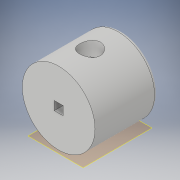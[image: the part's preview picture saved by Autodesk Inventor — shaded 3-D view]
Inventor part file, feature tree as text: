
AUTODESK INVENTOR PART (.ipt)
format: ipt  version: 2017 (Build 210142000, 142)  size: 147,456 bytes
history: native  units: in
note: dims shown in document units (in); Inventor stores cm internally (conversion verified against a paired STEP export)
features: sketch x4, extrude x2, plane x2, hole x2, chamfer x1, fillet x1
ambient origin geometry x8: Origin, YZ Plane, XZ Plane, XY Plane, X Axis, Y Axis, Z Axis, Center Point
bodies: Solid1 (feature_tree)
feature tree (12):
  extrude  "Extrusion1"  Depth=1.0in TaperAngle=0.0deg
  plane  "Work Plane2"
  sketch  "Sketch2"  dims[d3=0.5in d4=0.0in]
  sketch  "Sketch3"  dims[d5=0.5in d6=0.0in]
  hole  "Hole1"  [1 undecoded]
  hole  "Hole2"  [1 undecoded]
  extrude  "Extrusion2"  Depth=0.05in
  chamfer  "Chamfer1"  Distance=0.14in
  fillet  "Fillet1"  Radius=1.0in
  sketch  "Sketch1"  dims[d0=1.16in d1=1.0in d2=0.0in]
  plane  "Work Plane1"
  sketch  "Sketch4"  dims[d7=0.33in d8=0.75in d9=0.375in d10=0.25in d11=0.5635in d12=0.24in d13=60.0deg d14=0.33in d15=0.75in d16=0.375in d17=0.25in d18=0.5635in d19=0.24in d20=60.0deg d21=0.14in d22=0.14in d23=1.0in d24=0.0in d25=0.02in d26=0.125in d27=45.0deg d28=0.05in]
note: 2 required parameter values undecoded (feature->parameter linkage not recoverable at this tier; creation-order binding heuristic only, values carry confidence <= 0.55)
